# Revit family: AirTerminal_Diffuser-Swirl_Bradflo_PSD595
name_source: partatom
category: Air Terminals
units: mm (PartAtom-declared; Revit-internal decimal feet)

## family parameters
Cut with Voids When Loaded = No
Host = Face
OmniClass Number = 23.75.70.21.27.11
OmniClass Title = Diffusers, Registers, and Grilles
Part Type = Normal
Room Calculation Point = No
Round Connector Dimension = Use Diameter
Shared = No

## types (2) — shared parameters
Assembly Code = D3040100
Description = Swirl Diffuser with removable blades to alter discharge direction
DiffuserMaterial = Powdercoated-White
Manufacturer = Bradflo
ModifiedIssue_ANZRS = 20141013.53 $
URL = www.bradflo.com.au
zero-valued in all types: Cost, Default Elevation

## per-type parameters (varying)
| type | PSD595-24 | PSD595-48 | Type Comments |
| PSD595-48 | No | Yes | Swirl Diffuser with 48 Blades |
| PSD595-24 | Yes | No | Swirl Diffuser with 24 Blades |

## geometry (parser evidence)
native form markers: Sweep x3
no freeform markers — native parametric forms only
